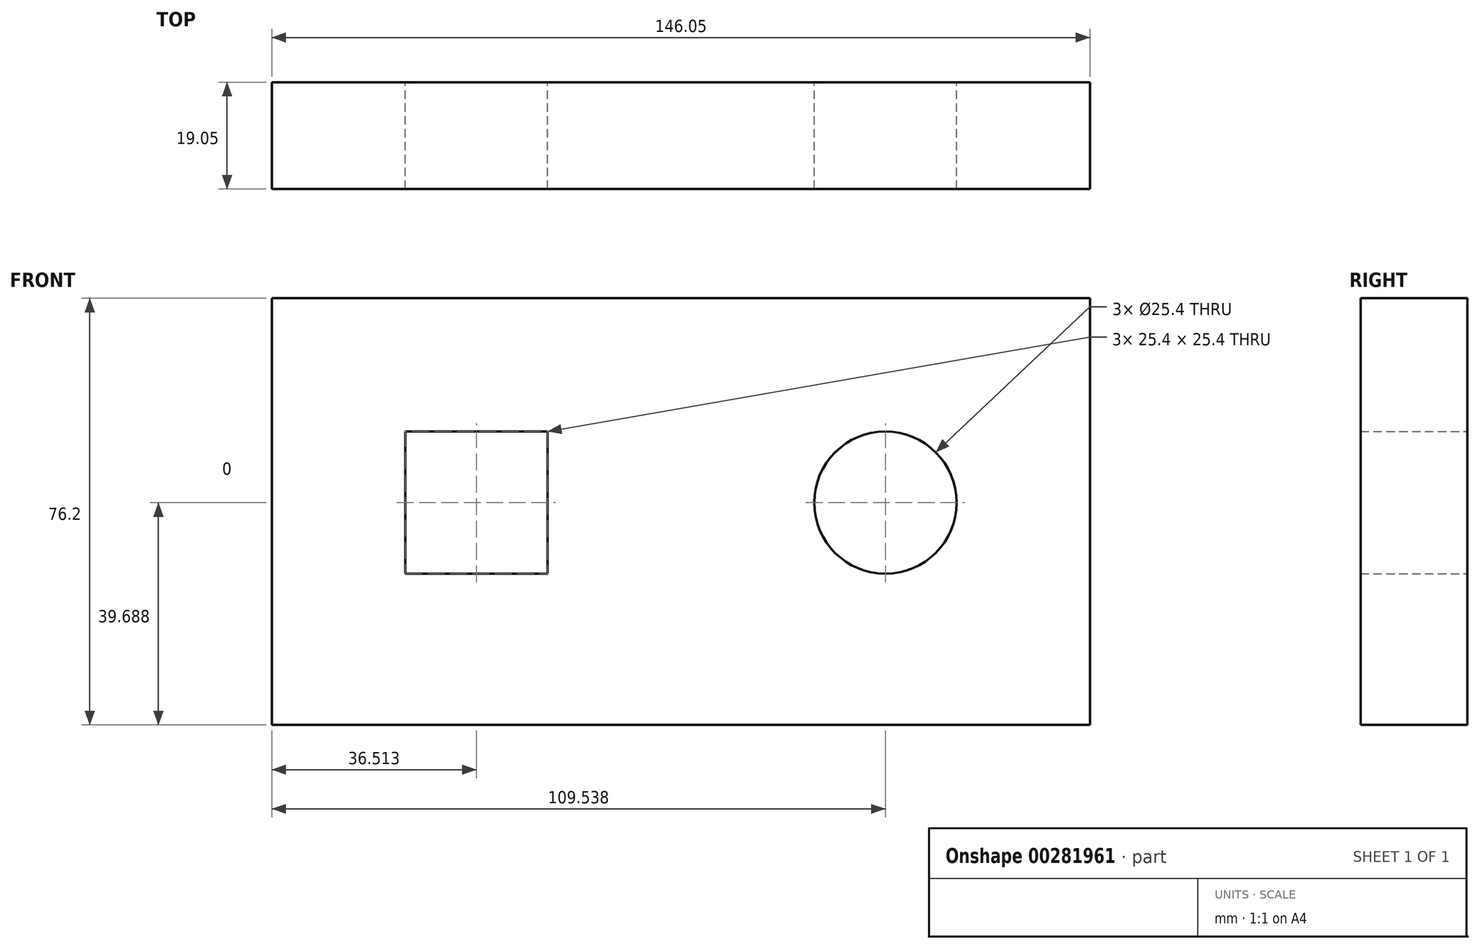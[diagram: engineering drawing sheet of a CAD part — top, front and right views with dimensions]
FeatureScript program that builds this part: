
annotation { "Feature Type Name" : "Feature", "Feature Type Description" : "" }
export const myFeature = defineFeature(function(context is Context, id is Id, definition is map)
    precondition{}
    {
        {
            var Q0;
            Q0=qCreatedBy(makeId("Front.planeOp"),FACE);
            var sketch = newSketch(context, id + "F0", { "sketchPlane" : qUnion([Q0])});
            skLineSegment(sketch, "E0.bottom", {"start": v(0, 0) * mm, "end": v(-146.05, 0) * mm});
            skLineSegment(sketch, "E0.top", {"start": v(0, 76.2) * mm, "end": v(-146.05, 76.2) * mm});
            skLineSegment(sketch, "E0.left", {"start": v(0, 0) * mm, "end": v(0, 76.2) * mm});
            skLineSegment(sketch, "E0.right", {"start": v(-146.05, 0) * mm, "end": v(-146.05, 76.2) * mm});
            skLineSegment(sketch, "E1.bottom", {"start": v(-122.24, 52.39) * mm, "end": v(-96.84, 52.39) * mm});
            skLineSegment(sketch, "E1.top", {"start": v(-122.24, 26.99) * mm, "end": v(-96.84, 26.99) * mm});
            skLineSegment(sketch, "E1.left", {"start": v(-122.24, 52.39) * mm, "end": v(-122.24, 26.99) * mm});
            skLineSegment(sketch, "E1.right", {"start": v(-96.84, 52.39) * mm, "end": v(-96.84, 26.99) * mm});
            skCircle(sketch, "E2", {"center": v(-36.51, 39.69) * mm, "radius": 12.7 * mm});
            skSolve(sketch);
        }
        {
            var Q0;
            Q0 = qSketchRegion(id + "F0", true);
            extrude(context, id + "F1", {"entities" : qUnion([Q0]), "depth" : 19.05 * mm});
        }
    });
